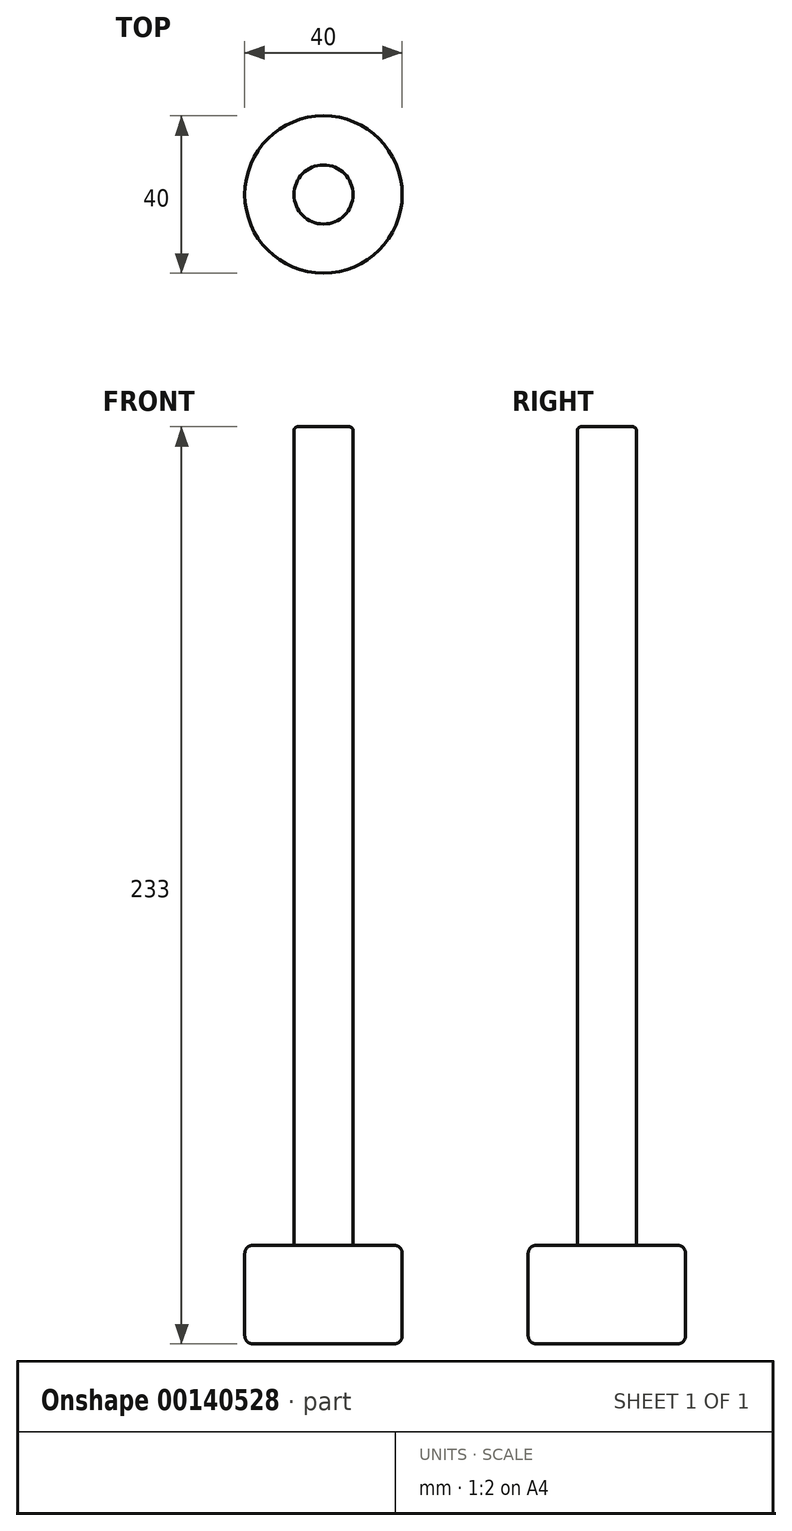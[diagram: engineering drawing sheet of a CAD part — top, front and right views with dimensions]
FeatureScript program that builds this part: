
annotation { "Feature Type Name" : "Feature", "Feature Type Description" : "" }
export const myFeature = defineFeature(function(context is Context, id is Id, definition is map)
    precondition{}
    {
        {
            var Q0;
            Q0=qCreatedBy(makeId("Top.planeOp"),FACE);
            var sketch = newSketch(context, id + "F0", { "sketchPlane" : qUnion([Q0])});
            skCircle(sketch, "E0", {"center": v(0, 0) * mm, "radius": 20 * mm});
            skSolve(sketch);
        }
        {
            var Q0;
            Q0 = qSketchRegion(id + "F0", true);
            extrude(context, id + "F1", {"entities" : qUnion([Q0]), "depth" : 25 * mm});
        }
        {
            var Q0;
            Q0=makeQuery(id+"F1.opExtrude","CAP_FACE",FACE,{"disambiguationData":[OSD([sQuery(id+"F0.wireOp",EDGE,"E0")])],"isStart":false});
            var sketch = newSketch(context, id + "F2", { "sketchPlane" : qUnion([Q0])});
            skCircle(sketch, "E1", {"center": v(0, 0) * mm, "radius": 7.5 * mm});
            skSolve(sketch);
        }
        {
            var Q0;
            Q0 = qSketchRegion(id + "F2", true);
            extrude(context, id + "F3", {"entities" : qUnion([Q0]), "operationType" : NewBodyOperationType.ADD, "depth" : 208 * mm});
        }
        {
            var Q0;
            Q0=makeQuery(id+"F1.opExtrude","CAP_EDGE",EDGE,{"disambiguationData":[OSD([sQuery(id+"F0.wireOp",EDGE,"E0")])],"isStart":true});
            var Q1;
            Q1=makeQuery(id+"F1.opExtrude","CAP_EDGE",EDGE,{"disambiguationData":[OSD([sQuery(id+"F0.wireOp",EDGE,"E0")])],"isStart":false});
            var Q2;
            Q2=makeQuery(id+"F3.opExtrude","CAP_EDGE",EDGE,{"disambiguationData":[OSD([sQuery(id+"F2.wireOp",EDGE,"E1")])],"isStart":true});
            fillet(context, id + "F4", {"entities" : qUnion([Q0, Q1, Q2]), "radius" : 2 * mm, "tangentPropagation" : true, "allowEdgeOverflow" : false});
        }
        {
            var Q0;
            Q0=makeQuery(id+"F3.opExtrude","CAP_EDGE",EDGE,{"disambiguationData":[OSD([sQuery(id+"F2.wireOp",EDGE,"E1")])],"isStart":false});
            fillet(context, id + "F5", {"entities" : qUnion([Q0]), "radius" : 1 * mm, "tangentPropagation" : true, "allowEdgeOverflow" : false});
        }
    });
